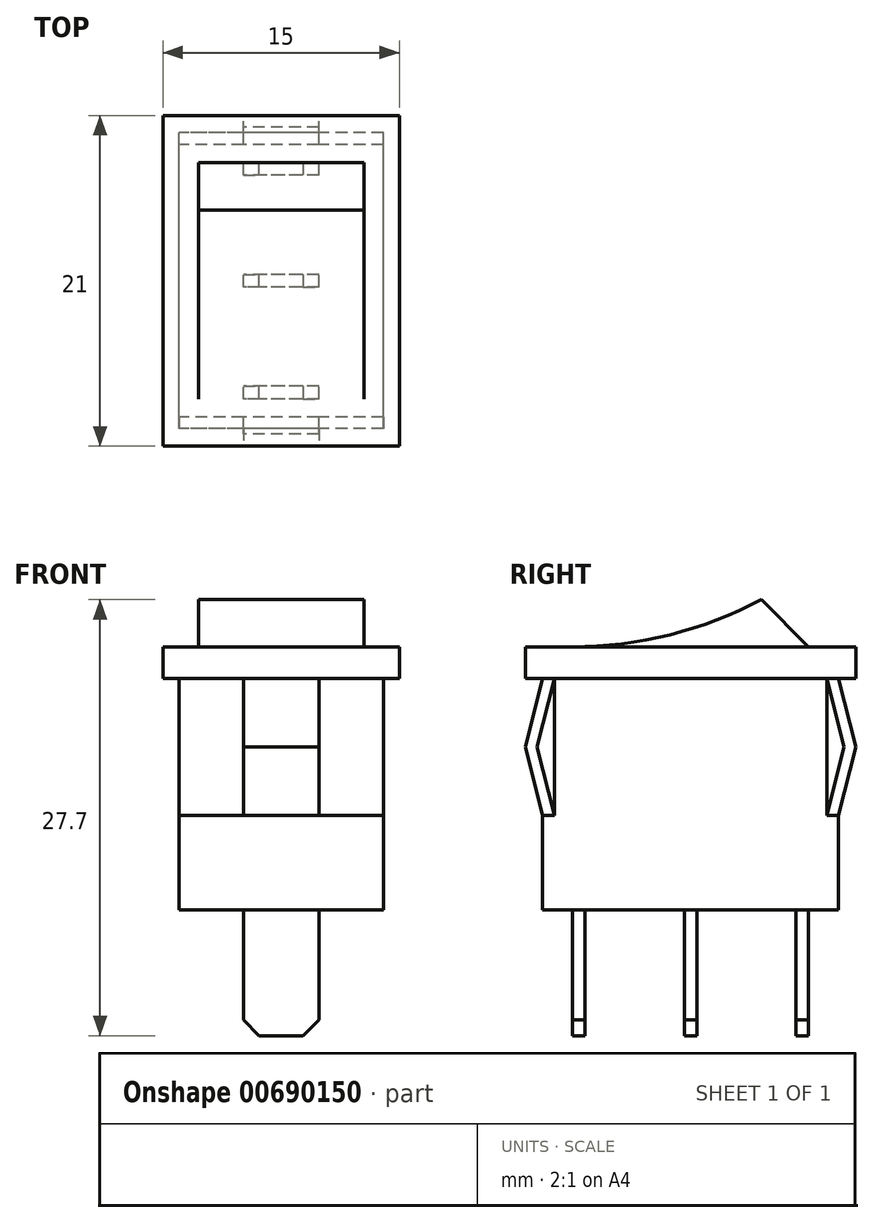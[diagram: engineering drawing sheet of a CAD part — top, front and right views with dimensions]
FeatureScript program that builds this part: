
annotation { "Feature Type Name" : "Feature", "Feature Type Description" : "" }
export const myFeature = defineFeature(function(context is Context, id is Id, definition is map)
    precondition{}
    {
        {
            var Q0;
            Q0=qCreatedBy(makeId("Right.planeOp"),FACE);
            var sketch = newSketch(context, id + "F0", { "sketchPlane" : qUnion([Q0])});
            skLineSegment(sketch, "E0.bottom", {"start": v(-10.5, 0) * mm, "end": v(10.5, 0) * mm});
            skLineSegment(sketch, "E0.top", {"start": v(-10.5, 2) * mm, "end": v(10.5, 2) * mm});
            skLineSegment(sketch, "E0.left", {"start": v(-10.5, 0) * mm, "end": v(-10.5, 2) * mm});
            skLineSegment(sketch, "E0.right", {"start": v(10.5, 0) * mm, "end": v(10.5, 2) * mm});
            skLineSegment(sketch, "E1", {"start": v(-8.65, 0) * mm, "end": v(-8.65, -8.7) * mm});
            skLineSegment(sketch, "E2", {"start": v(-8.65, -8.7) * mm, "end": v(-9.4, -8.7) * mm});
            skLineSegment(sketch, "E3", {"start": v(-9.4, -8.7) * mm, "end": v(-9.4, -14.7) * mm});
            skLineSegment(sketch, "E4", {"start": v(-9.4, -14.7) * mm, "end": v(9.4, -14.7) * mm});
            skLineSegment(sketch, "E5.MirrorCS", {"start": v(9.4, -8.7) * mm, "end": v(9.4, -14.7) * mm});
            skLineSegment(sketch, "E6.MirrorCS", {"start": v(8.65, 0) * mm, "end": v(8.65, -8.7) * mm});
            skLineSegment(sketch, "E7.MirrorCS", {"start": v(8.65, -8.7) * mm, "end": v(9.4, -8.7) * mm});
            skLineSegment(sketch, "E8", {"start": v(-7.5, -14.7) * mm, "end": v(-7.5, -22.7) * mm});
            skLineSegment(sketch, "E9", {"start": v(-7.5, -22.7) * mm, "end": v(-6.7, -22.7) * mm});
            skLineSegment(sketch, "E10", {"start": v(-6.7, -22.7) * mm, "end": v(-6.7, -14.7) * mm});
            skLineSegment(sketch, "E11", {"start": v(-0.4, -14.7) * mm, "end": v(-0.4, -22.7) * mm});
            skLineSegment(sketch, "E12", {"start": v(-0.4, -22.7) * mm, "end": v(0.4, -22.7) * mm});
            skLineSegment(sketch, "E13", {"start": v(0.4, -22.7) * mm, "end": v(0.4, -14.7) * mm});
            skLineSegment(sketch, "E14.MirrorCS", {"start": v(6.7, -22.7) * mm, "end": v(6.7, -14.7) * mm});
            skLineSegment(sketch, "E15.MirrorCS", {"start": v(7.5, -22.7) * mm, "end": v(6.7, -22.7) * mm});
            skLineSegment(sketch, "E16.MirrorCS", {"start": v(7.5, -14.7) * mm, "end": v(7.5, -22.7) * mm});
            skLineSegment(sketch, "E17", {"start": v(-8.65, 0) * mm, "end": v(-9.75, -4.35) * mm});
            skLineSegment(sketch, "E18", {"start": v(-9.75, -4.35) * mm, "end": v(-8.65, -8.7) * mm});
            skLineSegment(sketch, "E19", {"start": v(-9.4, -8.7) * mm, "end": v(-10.5, -4.35) * mm});
            skLineSegment(sketch, "E20", {"start": v(-10.5, -4.35) * mm, "end": v(-9.4, 0) * mm});
            skLineSegment(sketch, "E21.MirrorCS", {"start": v(8.65, 0) * mm, "end": v(9.75, -4.35) * mm});
            skLineSegment(sketch, "E22.MirrorCS", {"start": v(10.5, -4.35) * mm, "end": v(9.4, 0) * mm});
            skLineSegment(sketch, "E23.MirrorCS", {"start": v(9.4, -8.7) * mm, "end": v(10.5, -4.35) * mm});
            skLineSegment(sketch, "E24.MirrorCS", {"start": v(9.75, -4.35) * mm, "end": v(8.65, -8.7) * mm});
            skArc(sketch, "E25", {"start": v(-7.5, 2) * mm, "mid": v(-1.32, 2.76) * mm, "end": v(4.5, 5) * mm});
            skLineSegment(sketch, "E26", {"start": v(4.5, 5) * mm, "end": v(7.5, 2) * mm});
            skSolve(sketch);
        }
        {
            var Q0;
            {var subQ9=sQuery(id+"F0.wireOp",EDGE,"E1");Q0=makeQuery(id+"F0.imprint","IMPRINT",FACE,{"disambiguationData":[TD([[makeQuery(id+"F0.imprint","IMPRINT",EDGE,{"derivedFrom":subQ9}),1.0]])]});}
            extrude(context, id + "F1", {"entities" : qUnion([Q0]), "endBound" : BoundingType.SYMMETRIC, "depth" : 13 * mm, "offsetDistance" : 25 * mm});
        }
        {
            var Q0;
            {var subQ4=sQuery(id+"F0.wireOp",EDGE,"E0.left");Q0=makeQuery(id+"F0.imprint","IMPRINT",FACE,{"disambiguationData":[TD([[makeQuery(id+"F0.imprint","IMPRINT",EDGE,{"derivedFrom":subQ4}),-1.0]])]});}
            extrude(context, id + "F2", {"entities" : qUnion([Q0]), "operationType" : NewBodyOperationType.ADD, "endBound" : BoundingType.SYMMETRIC, "depth" : 15 * mm, "offsetDistance" : 25 * mm});
        }
        {
            var Q0;
            {var subQ0=sQuery(id+"F0.wireOp",EDGE,"E25");Q0=makeQuery(id+"F0.imprint","IMPRINT",FACE,{"disambiguationData":[TD([[makeQuery(id+"F0.imprint","IMPRINT",EDGE,{"derivedFrom":subQ0}),-1.0]])]});}
            extrude(context, id + "F3", {"entities" : qUnion([Q0]), "operationType" : NewBodyOperationType.ADD, "endBound" : BoundingType.SYMMETRIC, "depth" : 10.5 * mm, "offsetDistance" : 25 * mm});
        }
        {
            var Q0;
            Q0=makeQuery(id+"F0.imprint","IMPRINT",FACE,{"disambiguationData":[TD([[makeQuery(id+"F0.imprint","IMPRINT",EDGE,{"derivedFrom":sQuery(id+"F0.wireOp",EDGE,"E2")}),-1.0]])]});
            var Q1;
            Q1=makeQuery(id+"F0.imprint","IMPRINT",FACE,{"disambiguationData":[TD([[makeQuery(id+"F0.imprint","IMPRINT",EDGE,{"derivedFrom":sQuery(id+"F0.wireOp",EDGE,"E7.MirrorCS")}),1.0]])]});
            var Q2;
            {var subQ0=sQuery(id+"F0.wireOp",EDGE,"E14.MirrorCS");Q2=makeQuery(id+"F0.imprint","IMPRINT",FACE,{"disambiguationData":[TD([[makeQuery(id+"F0.imprint","IMPRINT",EDGE,{"derivedFrom":subQ0}),-1.0]])]});}
            var Q3;
            {var subQ2=sQuery(id+"F0.wireOp",EDGE,"E11");Q3=makeQuery(id+"F0.imprint","IMPRINT",FACE,{"disambiguationData":[TD([[makeQuery(id+"F0.imprint","IMPRINT",EDGE,{"derivedFrom":subQ2}),1.0]])]});}
            var Q4;
            {var subQ2=sQuery(id+"F0.wireOp",EDGE,"E8");Q4=makeQuery(id+"F0.imprint","IMPRINT",FACE,{"disambiguationData":[TD([[makeQuery(id+"F0.imprint","IMPRINT",EDGE,{"derivedFrom":subQ2}),1.0]])]});}
            extrude(context, id + "F4", {"entities" : qUnion([Q0, Q1, Q2, Q3, Q4]), "operationType" : NewBodyOperationType.ADD, "endBound" : BoundingType.SYMMETRIC, "depth" : 4.8 * mm, "offsetDistance" : 25 * mm});
        }
        {
            var Q0;
            Q0=makeQuery(id+"F4.opExtrude","CAP_EDGE",EDGE,{"disambiguationData":[OSD([sQuery(id+"F0.wireOp",EDGE,"E9")])],"isStart":false});
            var Q1;
            Q1=makeQuery(id+"F4.opExtrude","CAP_EDGE",EDGE,{"disambiguationData":[OSD([sQuery(id+"F0.wireOp",EDGE,"E12")])],"isStart":false});
            var Q2;
            Q2=makeQuery(id+"F4.opExtrude","CAP_EDGE",EDGE,{"disambiguationData":[OSD([sQuery(id+"F0.wireOp",EDGE,"E15.MirrorCS")])],"isStart":true});
            var Q3;
            Q3=makeQuery(id+"F4.opExtrude","CAP_EDGE",EDGE,{"disambiguationData":[OSD([sQuery(id+"F0.wireOp",EDGE,"E15.MirrorCS")])],"isStart":false});
            var Q4;
            Q4=makeQuery(id+"F4.opExtrude","CAP_EDGE",EDGE,{"disambiguationData":[OSD([sQuery(id+"F0.wireOp",EDGE,"E12")])],"isStart":true});
            var Q5;
            Q5=makeQuery(id+"F4.opExtrude","CAP_EDGE",EDGE,{"disambiguationData":[OSD([sQuery(id+"F0.wireOp",EDGE,"E9")])],"isStart":true});
            chamfer(context, id + "F5", {"entities" : qUnion([Q0, Q1, Q2, Q3, Q4, Q5]), "width" : 1 * mm, "tangentPropagation" : true});
        }
    });
